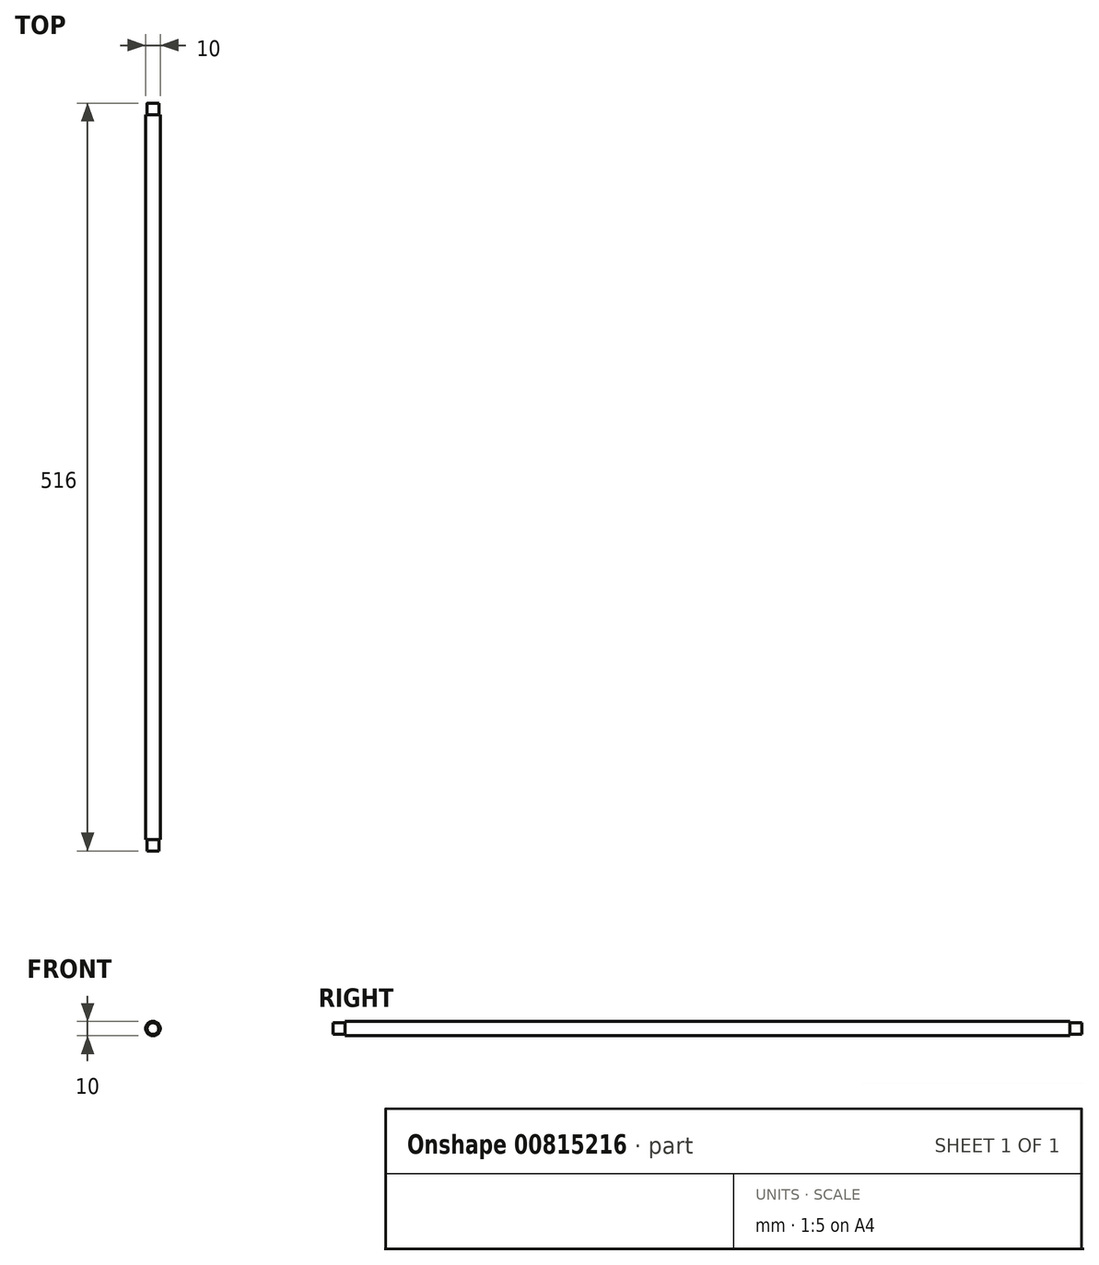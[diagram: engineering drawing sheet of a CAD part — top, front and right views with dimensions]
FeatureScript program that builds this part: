
annotation { "Feature Type Name" : "Feature", "Feature Type Description" : "" }
export const myFeature = defineFeature(function(context is Context, id is Id, definition is map)
    precondition{}
    {
        {
            var Q0;
            Q0=qCreatedBy(makeId("Front.planeOp"),FACE);
            var sketch = newSketch(context, id + "F0", { "sketchPlane" : qUnion([Q0])});
            skCircle(sketch, "E0", {"center": v(0, 0) * mm, "radius": 5 * mm});
            skSolve(sketch);
        }
        {
            var Q0;
            Q0 = qSketchRegion(id + "F0", true);
            extrude(context, id + "F1", {"entities" : qUnion([Q0]), "endBound" : BoundingType.SYMMETRIC, "oppositeDirection" : true, "depth" : 516 * mm, "offsetDistance" : 25 * mm});
        }
        {
            var Q0;
            Q0=makeQuery(id+"F1.opExtrude","CAP_FACE",FACE,{"disambiguationData":[OSD([sQuery(id+"F0.wireOp",EDGE,"E0")])],"isStart":true});
            var sketch = newSketch(context, id + "F2", { "sketchPlane" : qUnion([Q0])});
            skCircle(sketch, "E1", {"center": v(0, 0) * mm, "radius": 4 * mm});
            skCircle(sketch, "E2.0", {"center": v(0, 0) * mm, "radius": 9 * mm});
            skSolve(sketch);
        }
        {
            var Q0;
            Q0 = qSketchRegion(id + "F2", true);
            extrude(context, id + "F3", {"entities" : qUnion([Q0]), "operationType" : NewBodyOperationType.REMOVE, "oppositeDirection" : true, "depth" : 8 * mm, "offsetDistance" : 25 * mm});
        }
        {
            var Q0;
            Q0=makeQuery(id+"F1.opExtrude","CAP_FACE",FACE,{"disambiguationData":[OSD([sQuery(id+"F0.wireOp",EDGE,"E0")])],"isStart":false});
            var sketch = newSketch(context, id + "F4", { "sketchPlane" : qUnion([Q0])});
            skCircle(sketch, "E3.0", {"center": v(0, 0) * mm, "radius": 5 * mm});
            skCircle(sketch, "E4", {"center": v(0, 0) * mm, "radius": 4 * mm});
            skSolve(sketch);
        }
        {
            var Q0;
            Q0 = qSketchRegion(id + "F4", true);
            extrude(context, id + "F5", {"entities" : qUnion([Q0]), "operationType" : NewBodyOperationType.REMOVE, "oppositeDirection" : true, "depth" : 8 * mm, "offsetDistance" : 25 * mm});
        }
    });
